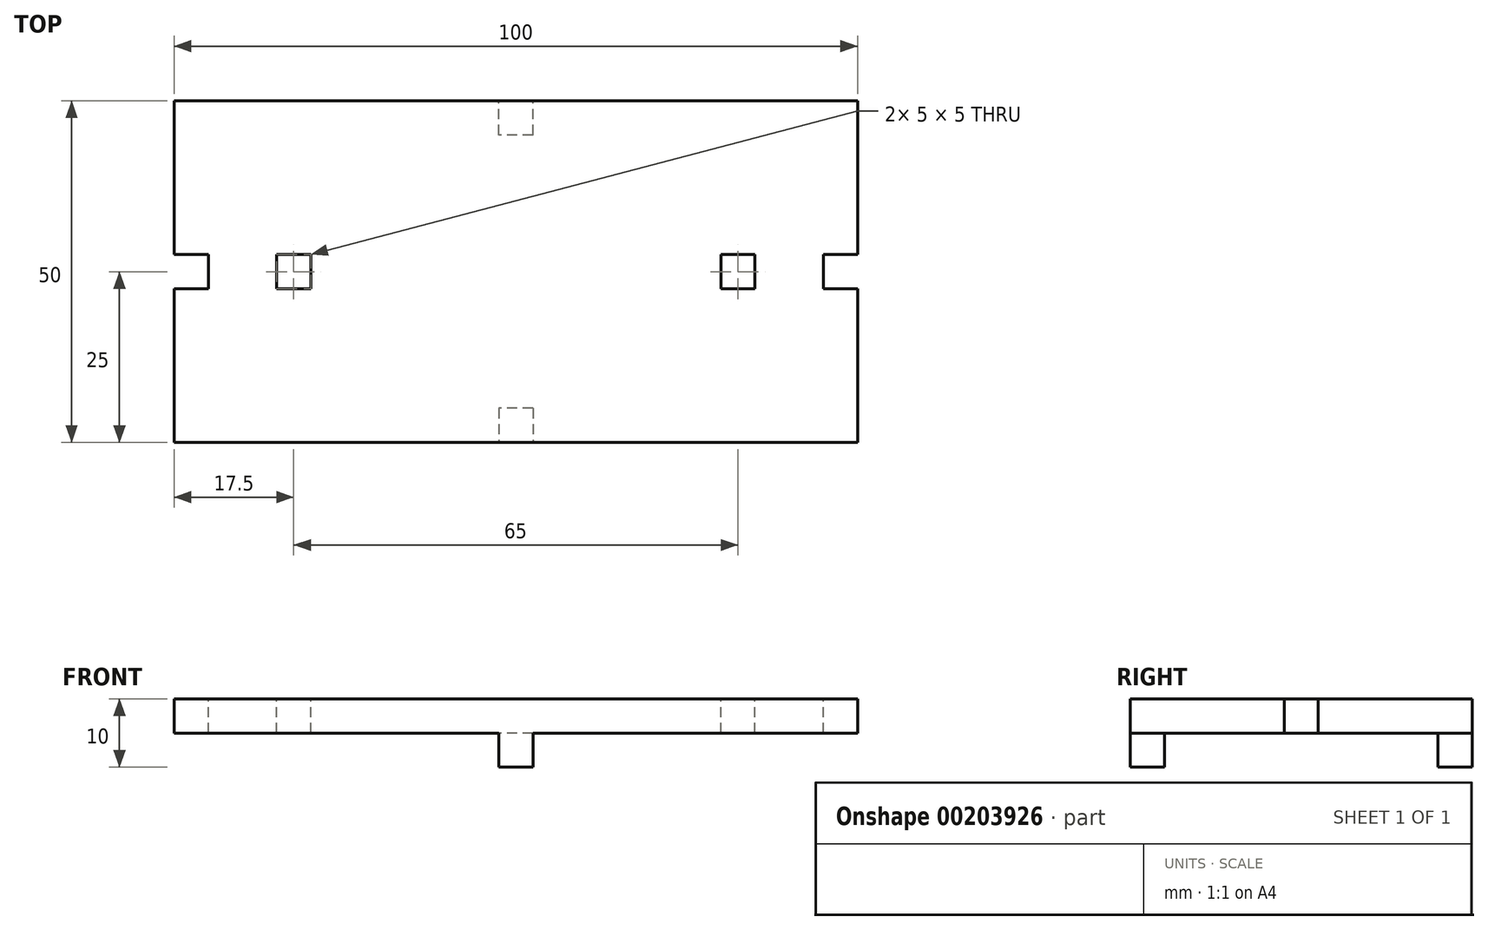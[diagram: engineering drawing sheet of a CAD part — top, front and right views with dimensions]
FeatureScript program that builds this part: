
annotation { "Feature Type Name" : "Feature", "Feature Type Description" : "" }
export const myFeature = defineFeature(function(context is Context, id is Id, definition is map)
    precondition{}
    {
        {
            var Q0;
            Q0=qCreatedBy(makeId("Top.planeOp"),FACE);
            var sketch = newSketch(context, id + "F0", { "sketchPlane" : qUnion([Q0])});
            skLineSegment(sketch, "E0.bottom", {"start": v(50, 25) * mm, "end": v(-50, 25) * mm});
            skLineSegment(sketch, "E0.top", {"start": v(50, -25) * mm, "end": v(-50, -25) * mm});
            skLineSegment(sketch, "E0.left", {"start": v(50, 25) * mm, "end": v(50, -25) * mm});
            skLineSegment(sketch, "E0.right", {"start": v(-50, 25) * mm, "end": v(-50, -25) * mm});
            skPoint(sketch, "E0.middle", {"position": v(0, 0) * mm});
            skSolve(sketch);
        }
        {
            var Q0;
            Q0=qSketchRegion(id+"F0",true);
            extrude(context, id + "F1", {"entities" : qUnion([Q0]), "depth" : 5 * mm});
        }
        {
            var Q0;
            Q0=makeQuery(id+"F1.opExtrude","SWEPT_FACE",FACE,{"disambiguationData":[OSD([sQuery(id+"F0.wireOp",EDGE,"E0.top")])]});
            var sketch = newSketch(context, id + "F2", { "sketchPlane" : qUnion([Q0])});
            skLineSegment(sketch, "E1", {"start": v(-2.5, 0) * mm, "end": v(-2.5, -5) * mm});
            skLineSegment(sketch, "E2", {"start": v(-2.5, -5) * mm, "end": v(2.5, -5) * mm});
            skLineSegment(sketch, "E3", {"start": v(2.5, -5) * mm, "end": v(2.5, 0) * mm});
            skLineSegment(sketch, "E4", {"start": v(2.5, 0) * mm, "end": v(-2.5, 0) * mm});
            skSolve(sketch);
        }
        {
            var Q0;
            Q0=qSketchRegion(id+"F2",true);
            extrude(context, id + "F3", {"entities" : qUnion([Q0]), "operationType" : NewBodyOperationType.ADD, "oppositeDirection" : true, "depth" : 5 * mm});
        }
        {
            var Q0;
            Q0=makeQuery(id+"F1.opExtrude","SWEPT_FACE",FACE,{"disambiguationData":[OSD([sQuery(id+"F0.wireOp",EDGE,"E0.bottom")])]});
            var sketch = newSketch(context, id + "F4", { "sketchPlane" : qUnion([Q0])});
            skLineSegment(sketch, "E5", {"start": v(-2.5, 0) * mm, "end": v(-2.5, -5) * mm});
            skLineSegment(sketch, "E6", {"start": v(-2.5, -5) * mm, "end": v(2.5, -5) * mm});
            skLineSegment(sketch, "E7", {"start": v(2.5, -5) * mm, "end": v(2.5, 0) * mm});
            skLineSegment(sketch, "E8", {"start": v(2.5, 0) * mm, "end": v(-2.5, 0) * mm});
            skSolve(sketch);
        }
        {
            var Q0;
            Q0=qSketchRegion(id+"F4",true);
            extrude(context, id + "F5", {"entities" : qUnion([Q0]), "operationType" : NewBodyOperationType.ADD, "oppositeDirection" : true, "depth" : 5 * mm});
        }
        {
            var Q0;
            Q0=makeQuery(id+"F1.opExtrude","CAP_FACE",FACE,{"disambiguationData":[OSD([sQuery(id+"F0.wireOp",EDGE,"E0.bottom"),sQuery(id+"F0.wireOp",EDGE,"E0.top"),sQuery(id+"F0.wireOp",EDGE,"E0.left"),sQuery(id+"F0.wireOp",EDGE,"E0.right")])],"isStart":false});
            var sketch = newSketch(context, id + "F6", { "sketchPlane" : qUnion([Q0])});
            skLineSegment(sketch, "E9", {"start": v(0, 0) * mm, "end": v(-50, 0) * mm, "construction": true});
            skLineSegment(sketch, "E10", {"start": v(-50, 0) * mm, "end": v(-50, 2.5) * mm});
            skLineSegment(sketch, "E11", {"start": v(-50, 2.5) * mm, "end": v(-45, 2.5) * mm});
            skLineSegment(sketch, "E12", {"start": v(-45, 2.5) * mm, "end": v(-45, -2.5) * mm});
            skLineSegment(sketch, "E13", {"start": v(-45, -2.5) * mm, "end": v(-50, -2.5) * mm});
            skLineSegment(sketch, "E14", {"start": v(-50, -2.5) * mm, "end": v(-50, 0) * mm});
            skLineSegment(sketch, "E15.bottom", {"start": v(-35, 2.5) * mm, "end": v(-30, 2.5) * mm});
            skLineSegment(sketch, "E15.top", {"start": v(-35, -2.5) * mm, "end": v(-30, -2.5) * mm});
            skLineSegment(sketch, "E15.left", {"start": v(-35, 2.5) * mm, "end": v(-35, -2.5) * mm});
            skLineSegment(sketch, "E15.right", {"start": v(-30, 2.5) * mm, "end": v(-30, -2.5) * mm});
            skPoint(sketch, "E15.middle", {"position": v(-32.5, 0) * mm});
            skLineSegment(sketch, "E16", {"start": v(0, -25) * mm, "end": v(0, 25) * mm, "construction": true});
            skLineSegment(sketch, "E17.MirrorCS", {"start": v(30, 2.5) * mm, "end": v(30, -2.5) * mm});
            skLineSegment(sketch, "E18.MirrorCS", {"start": v(35, 2.5) * mm, "end": v(30, 2.5) * mm});
            skLineSegment(sketch, "E19.MirrorCS", {"start": v(35, 2.5) * mm, "end": v(35, -2.5) * mm});
            skLineSegment(sketch, "E20.MirrorCS", {"start": v(35, -2.5) * mm, "end": v(30, -2.5) * mm});
            skLineSegment(sketch, "E21.MirrorCS", {"start": v(45, -2.5) * mm, "end": v(50, -2.5) * mm});
            skLineSegment(sketch, "E22.MirrorCS", {"start": v(45, 2.5) * mm, "end": v(45, -2.5) * mm});
            skLineSegment(sketch, "E23.MirrorCS", {"start": v(50, -2.5) * mm, "end": v(50, 0) * mm});
            skLineSegment(sketch, "E24.MirrorCS", {"start": v(50, 0) * mm, "end": v(50, 2.5) * mm});
            skLineSegment(sketch, "E25.MirrorCS", {"start": v(50, 2.5) * mm, "end": v(45, 2.5) * mm});
            skSolve(sketch);
        }
        {
            var Q0;
            Q0=qSketchRegion(id+"F6",true);
            extrude(context, id + "F7", {"entities" : qUnion([Q0]), "operationType" : NewBodyOperationType.REMOVE, "endBound" : BoundingType.UP_TO_NEXT, "oppositeDirection" : true, "depth" : 25 * mm});
        }
    });
